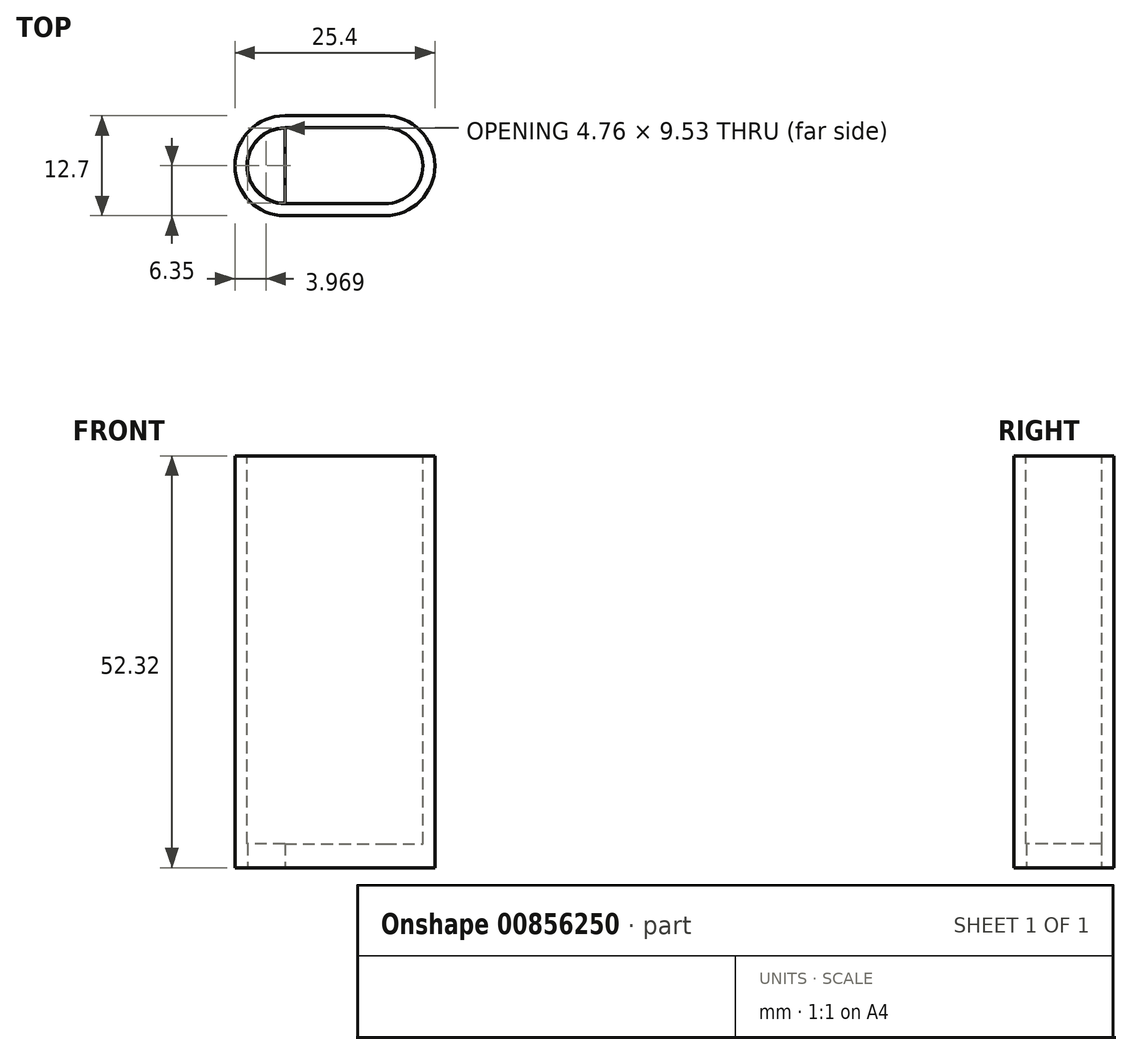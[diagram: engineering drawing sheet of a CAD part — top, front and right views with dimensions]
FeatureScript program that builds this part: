
annotation { "Feature Type Name" : "Feature", "Feature Type Description" : "" }
export const myFeature = defineFeature(function(context is Context, id is Id, definition is map)
    precondition{}
    {
        {
            var Q0;
            Q0=qCreatedBy(makeId("Top.planeOp"),FACE);
            var sketch = newSketch(context, id + "F0", { "sketchPlane" : qUnion([Q0])});
            skLineSegment(sketch, "E0.bottom", {"start": v(0, 0) * mm, "end": v(12.7, 0) * mm});
            skLineSegment(sketch, "E0.top", {"start": v(0, -12.7) * mm, "end": v(12.7, -12.7) * mm});
            skLineSegment(sketch, "E0.left", {"start": v(0, 0) * mm, "end": v(0, -12.7) * mm});
            skLineSegment(sketch, "E0.right", {"start": v(12.7, 0) * mm, "end": v(12.7, -12.7) * mm});
            skArc(sketch, "E1", {"start": v(12.7, -12.7) * mm, "mid": v(19.05, -6.35) * mm, "end": v(12.7, 0) * mm});
            skLineSegment(sketch, "E2", {"start": v(6.35, 0) * mm, "end": v(6.35, -12.7) * mm});
            skArc(sketch, "E3.MirrorC", {"start": v(0, -12.7) * mm, "mid": v(-6.35, -6.35) * mm, "end": v(0, 0) * mm});
            skArc(sketch, "E4.0", {"start": v(12.7, -11.11) * mm, "mid": v(17.46, -6.35) * mm, "end": v(12.7, -1.59) * mm});
            skLineSegment(sketch, "E4.1", {"start": v(0, -11.11) * mm, "end": v(12.7, -11.11) * mm});
            skArc(sketch, "E4.2", {"start": v(0, -11.11) * mm, "mid": v(-4.76, -6.35) * mm, "end": v(0, -1.59) * mm});
            skLineSegment(sketch, "E4.3", {"start": v(0, -1.59) * mm, "end": v(12.7, -1.59) * mm});
            skSolve(sketch);
        }
        {
            var Q0;
            Q0 = qSketchRegion(id + "F0", true);
            var Q1;
            {var subQ4=sQuery(id+"F0.wireOp",EDGE,"E4.3");var subQ6=sQuery(id+"F0.wireOp",EDGE,"E2");var subQ7=makeQuery(id+"F0.imprint","INTERSECT",VERTEX,{"derivedFrom":[subQ6,subQ4]});Q1=makeQuery(id+"F0.imprint","IMPRINT",FACE,{"disambiguationData":[TD([[makeQuery(id+"F0.imprint","IMPRINT",EDGE,{"disambiguationData":[TD([[subQ7,-1.0]])],"derivedFrom":subQ6}),1.0]])]});}
            var Q2;
            {var subQ4=sQuery(id+"F0.wireOp",EDGE,"E4.3");var subQ6=sQuery(id+"F0.wireOp",EDGE,"E2");var subQ7=makeQuery(id+"F0.imprint","INTERSECT",VERTEX,{"derivedFrom":[subQ6,subQ4]});Q2=makeQuery(id+"F0.imprint","IMPRINT",FACE,{"disambiguationData":[TD([[makeQuery(id+"F0.imprint","IMPRINT",EDGE,{"disambiguationData":[TD([[subQ7,-1.0]])],"derivedFrom":subQ6}),-1.0]])]});}
            var Q3;
            {var subQ0=sQuery(id+"F0.wireOp",EDGE,"E4.2");Q3=makeQuery(id+"F0.imprint","IMPRINT",FACE,{"disambiguationData":[TD([[makeQuery(id+"F0.imprint","IMPRINT",EDGE,{"derivedFrom":subQ0}),-1.0]])]});}
            var Q4;
            {var subQ0=sQuery(id+"F0.wireOp",EDGE,"E4.0");Q4=makeQuery(id+"F0.imprint","IMPRINT",FACE,{"disambiguationData":[TD([[makeQuery(id+"F0.imprint","IMPRINT",EDGE,{"derivedFrom":subQ0}),1.0]])]});}
            extrude(context, id + "F1", {"entities" : qUnion([Q0, Q1, Q2, Q3, Q4]), "depth" : 52.32 * mm, "offsetDistance" : 25.4 * mm});
        }
        {
            var Q0;
            Q0=makeQuery(id+"F1.opExtrude","CAP_FACE",FACE,{"disambiguationData":[OSD([sQuery(id+"F0.wireOp",EDGE,"E0.bottom"),sQuery(id+"F0.wireOp",EDGE,"E0.top"),sQuery(id+"F0.wireOp",EDGE,"E1"),sQuery(id+"F0.wireOp",EDGE,"E3.MirrorC")])],"isStart":false});
            var sketch = newSketch(context, id + "F2", { "sketchPlane" : qUnion([Q0])});
            skLineSegment(sketch, "E5.0", {"start": v(0, -1.52) * mm, "end": v(12.7, -1.52) * mm});
            skArc(sketch, "E5.1", {"start": v(0, -11.18) * mm, "mid": v(-4.83, -6.35) * mm, "end": v(0, -1.52) * mm});
            skLineSegment(sketch, "E5.2", {"start": v(0, -11.18) * mm, "end": v(12.7, -11.18) * mm});
            skArc(sketch, "E5.3", {"start": v(12.7, -11.18) * mm, "mid": v(17.53, -6.35) * mm, "end": v(12.7, -1.52) * mm});
            skSolve(sketch);
        }
        {
            var Q0;
            Q0 = qSketchRegion(id + "F2", true);
            extrude(context, id + "F3", {"entities" : qUnion([Q0]), "operationType" : NewBodyOperationType.REMOVE, "oppositeDirection" : true, "depth" : 49.28 * mm, "offsetDistance" : 25.4 * mm});
        }
    });
